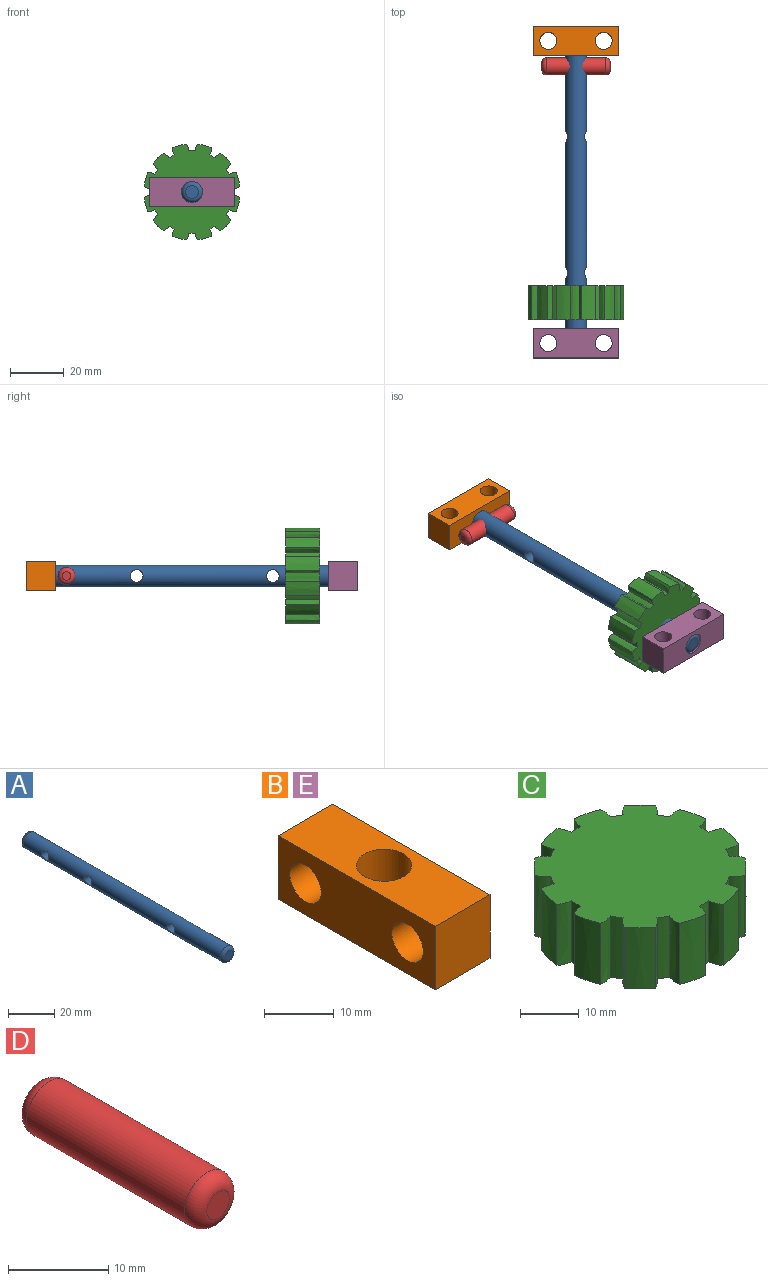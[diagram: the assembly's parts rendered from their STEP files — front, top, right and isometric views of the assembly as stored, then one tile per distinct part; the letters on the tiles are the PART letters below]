
ASSEMBLY  parts=5 mates=4
PART A: 8 faces, bbox 8.6x123.8x8.6 mm
  f0: cylinder r=3.97mm len=120.65mm, axis (0,1,0), area 2896.2mm2, adj f3,f4,f5,f6,f7
  f1: plane 4.76x4.76mm, normal (0,-1,0), area 17.8mm2, adj f4
  f2: plane 4.76x4.76mm, normal (0,1,0), area 17.8mm2, adj f3
  f3: torus R=2.38mm, axis (0,-1,0), area 53.1mm2, adj f0,f2
  f4: torus R=2.38mm, axis (0,-1,0), area 53.1mm2, adj f0,f1
  f5: cylinder r=2.38mm len=7.94mm, axis (1,0,0), area 107.2mm2, adj f0
  f6: cylinder r=2.38mm len=7.94mm, axis (1,0,0), area 107.2mm2, adj f0
  f7: cylinder r=2.38mm len=7.94mm, axis (1,0,0), area 107.2mm2, adj f0
PART B: 9 faces, bbox 11.1x31.8x11.1 mm
  f0: plane 31.75x11.11mm, normal (-1,0,0), area 289.5mm2, adj f1,f3,f4,f5,f7,f8
  f1: plane 31.75x11.11mm, normal (0,0,-1), area 303.3mm2, adj f0,f2,f4,f5,f6
  f2: plane 31.75x11.11mm, normal (1,0,0), area 289.5mm2, adj f1,f3,f4,f5,f7,f8
  f3: plane 31.75x11.11mm, normal (0,0,1), area 303.3mm2, adj f0,f2,f4,f5,f6
  f4: plane 11.11x11.11mm, normal (0,-1,0), area 123.5mm2, adj f0,f1,f2,f3
  f5: plane 11.11x11.11mm, normal (0,1,0), area 123.5mm2, adj f0,f1,f2,f3
  f6: cylinder r=3.97mm len=11.11mm, axis (0,0,1), area 277.1mm2, adj f1,f3
  f7: cylinder r=3.17mm len=11.11mm, axis (1,0,0), area 221.7mm2, adj f0,f2
  f8: cylinder r=3.17mm len=11.11mm, axis (1,0,0), area 221.7mm2, adj f0,f2
PART C: 50 faces, bbox 35.8x35.8x12.7 mm
  f0: extruded ~12.7x2.07mm, area 34.4mm2, adj f1,f47,f48,f49
  f1: extruded ~12.7x3.7mm, area 66.6mm2, adj f0,f2,f48,f49
  f2: extruded ~12.7x2.07mm, area 34.4mm2, adj f1,f3,f48,f49
  f3: extruded ~12.7x1.97mm, area 29mm2, adj f2,f4,f48,f49
  f4: extruded ~12.7x2.63mm, area 34.4mm2, adj f3,f5,f48,f49
  f5: extruded ~12.7x5.05mm, area 66.6mm2, adj f4,f6,f48,f49
  f6: extruded ~12.7x2.5mm, area 34.4mm2, adj f5,f7,f48,f49
  f7: extruded ~12.7x2.28mm, area 29mm2, adj f6,f8,f48,f49
  f8: extruded ~12.7x2.5mm, area 34.4mm2, adj f7,f9,f48,f49
  f9: extruded ~12.7x5.05mm, area 66.6mm2, adj f8,f10,f48,f49
  f10: extruded ~12.7x2.63mm, area 34.4mm2, adj f9,f11,f48,f49
  f11: extruded ~12.7x1.97mm, area 29mm2, adj f10,f12,f48,f49
  f12: extruded ~12.7x2.07mm, area 34.4mm2, adj f11,f13,f48,f49
  f13: extruded ~12.7x3.7mm, area 66.6mm2, adj f12,f14,f48,f49
  f14: extruded ~12.7x2.07mm, area 34.4mm2, adj f13,f15,f48,f49
  f15: extruded ~12.7x1.97mm, area 29mm2, adj f14,f16,f48,f49
  f16: extruded ~12.7x2.63mm, area 34.4mm2, adj f15,f17,f48,f49
  f17: extruded ~12.7x5.05mm, area 66.6mm2, adj f16,f18,f48,f49
  f18: extruded ~12.7x2.5mm, area 34.4mm2, adj f17,f19,f48,f49
  f19: extruded ~12.7x2.28mm, area 29mm2, adj f18,f20,f48,f49
  f20: extruded ~12.7x2.5mm, area 34.4mm2, adj f19,f21,f48,f49
  f21: extruded ~12.7x5.05mm, area 66.6mm2, adj f20,f22,f48,f49
  f22: extruded ~12.7x2.63mm, area 34.4mm2, adj f21,f23,f48,f49
  f23: extruded ~12.7x1.97mm, area 29mm2, adj f22,f24,f48,f49
  f24: extruded ~12.7x2.07mm, area 34.4mm2, adj f23,f25,f48,f49
  f25: extruded ~12.7x3.7mm, area 66.6mm2, adj f24,f26,f48,f49
  f26: extruded ~12.7x2.07mm, area 34.4mm2, adj f25,f27,f48,f49
  f27: extruded ~12.7x1.97mm, area 29mm2, adj f26,f28,f48,f49
  f28: extruded ~12.7x2.63mm, area 34.4mm2, adj f27,f29,f48,f49
  f29: extruded ~12.7x5.05mm, area 66.6mm2, adj f28,f30,f48,f49
  f30: extruded ~12.7x2.5mm, area 34.4mm2, adj f29,f31,f48,f49
  f31: extruded ~12.7x2.28mm, area 29mm2, adj f30,f32,f48,f49
  f32: extruded ~12.7x2.5mm, area 34.4mm2, adj f31,f33,f48,f49
  f33: extruded ~12.7x5.05mm, area 66.6mm2, adj f32,f34,f48,f49
  f34: extruded ~12.7x2.63mm, area 34.4mm2, adj f33,f35,f48,f49
  f35: extruded ~12.7x1.97mm, area 29mm2, adj f34,f36,f48,f49
  f36: extruded ~12.7x2.07mm, area 34.4mm2, adj f35,f37,f48,f49
  f37: extruded ~12.7x3.7mm, area 66.6mm2, adj f36,f38,f48,f49
  f38: extruded ~12.7x2.07mm, area 34.4mm2, adj f37,f39,f48,f49
  f39: extruded ~12.7x1.97mm, area 29mm2, adj f38,f40,f48,f49
  f40: extruded ~12.7x2.63mm, area 34.4mm2, adj f39,f41,f48,f49
  f41: extruded ~12.7x5.05mm, area 66.6mm2, adj f40,f42,f48,f49
  f42: extruded ~12.7x2.5mm, area 34.4mm2, adj f41,f43,f48,f49
  f43: extruded ~12.7x2.28mm, area 29mm2, adj f42,f44,f48,f49
  f44: extruded ~12.7x2.5mm, area 34.4mm2, adj f43,f45,f48,f49
  f45: extruded ~12.7x5.05mm, area 66.6mm2, adj f44,f46,f48,f49
  f46: extruded ~12.7x2.63mm, area 34.4mm2, adj f45,f47,f48,f49
  f47: extruded ~12.7x1.97mm, area 29mm2, adj f0,f46,f48,f49
  f48: plane 35.76x35.76mm, normal (0,0,-1), area 926.3mm2, adj f0,f1,f2,f3,f4,f5,f6,f7
  f49: plane 35.76x35.76mm, normal (0,0,1), area 926.3mm2, adj f0,f1,f2,f3,f4,f5,f6,f7
PART D: 5 faces, bbox 6.9x25.4x6.9 mm
  f0: cylinder r=3.17mm len=22.23mm, axis (0,1,0), area 443.4mm2, adj f3,f4
  f1: plane 3.18x3.18mm, normal (0,-1,0), area 7.9mm2, adj f4
  f2: plane 3.18x3.18mm, normal (0,1,0), area 7.9mm2, adj f3
  f3: torus R=1.59mm, axis (0,-1,0), area 40.7mm2, adj f0,f2
  f4: torus R=1.59mm, axis (0,-1,0), area 40.7mm2, adj f0,f1
PART E: same geometry as B
PLACE A t=(-29.4,31.78,-19.75)mm fixed
PLACE B rot(axis=(-0.58,0.58,0.58),120deg) t=(-45.27,20.66,-14.19)mm
PLACE C rot(axis=(-1,0,0),90deg) t=(-29.4,-65.06,-19.75)mm
PLACE D rot(axis=(0.58,0.58,-0.58),120deg) t=(-16.7,16.69,-19.75)mm
PLACE E rot(axis=(0.58,-0.58,0.58),120deg) t=(-45.27,-80.94,-25.3)mm
MATE fastened C.f49 <-> A.f0  axis (0,1,0) through (-29.4,-65.06,-19.75)mm
MATE revolute B.f6 <-> A.f0  axis (0,1,0) through (-29.4,31.78,-19.75)mm
MATE revolute E.f6 <-> A.f0  axis (0,-1,0) through (-29.4,-92.05,-19.75)mm
MATE fastened D.f0 <-> A.f7  axis (1,0,0) through (-29.4,16.69,-19.75)mm
